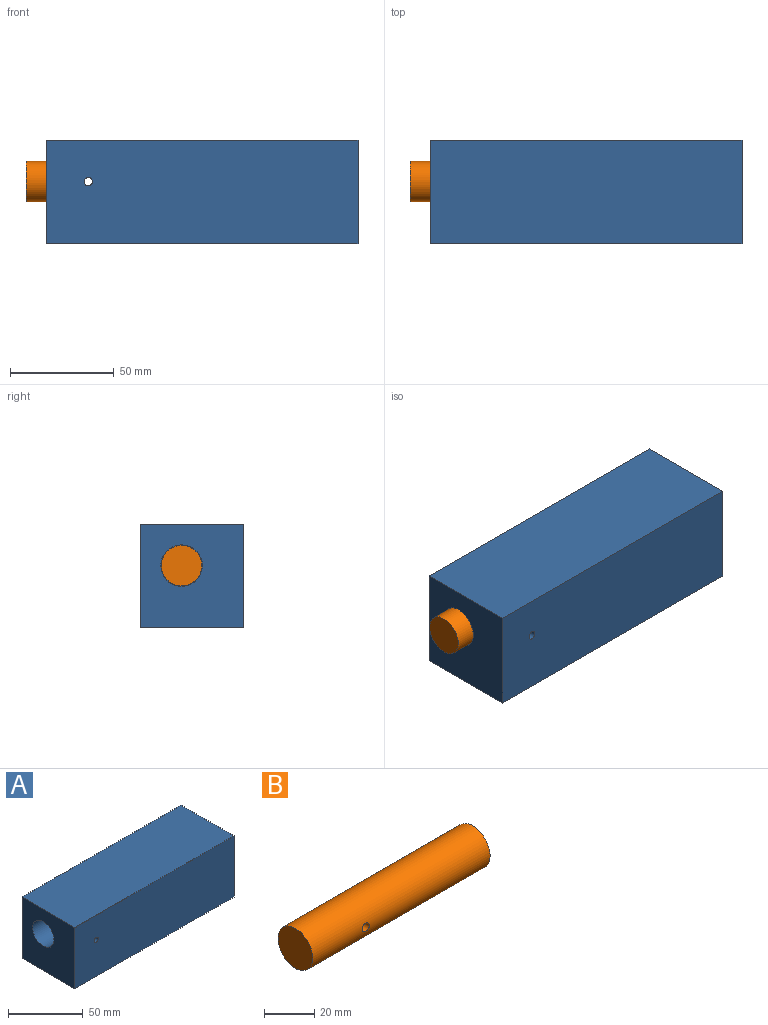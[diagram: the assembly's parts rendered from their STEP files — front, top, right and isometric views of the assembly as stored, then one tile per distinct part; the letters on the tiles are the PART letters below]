
ASSEMBLY  parts=2 mates=1
PART A: 10 faces, bbox 150x50x50 mm
  f0: cylinder r=2mm len=10.2mm, axis (0,-1,0), area 126.9mm2, adj f6,f8
  f1: plane 150x50mm, normal (0,0,1), area 7500mm2, adj f2,f4,f5,f6
  f2: plane 50x50mm, normal (-1,0,0), area 2185.8mm2, adj f1,f3,f5,f6,f8
  f3: plane 150x50mm, normal (0,0,-1), area 7500mm2, adj f2,f4,f5,f6
  f4: plane 50x50mm, normal (1,0,0), area 2500mm2, adj f1,f3,f5,f6
  f5: plane 150x50mm, normal (0,-1,0), area 7487.4mm2, adj f1,f2,f3,f4,f7
  f6: plane 150x50mm, normal (0,1,0), area 7487.4mm2, adj f0,f1,f2,f3,f4
  f7: cylinder r=2mm len=20.2mm, axis (0,-1,0), area 252.6mm2, adj f5,f8
  f8: cylinder r=10mm len=100mm, axis (-1,0,0), area 6257.9mm2, adj f0,f2,f7,f9
  f9: plane 20x20mm, normal (-1,0,0), area 314.2mm2, adj f8
PART B: 4 faces, bbox 100x19.5x19.5 mm
  f0: cylinder r=9.75mm len=100mm, axis (-1,0,0), area 6100.8mm2, adj f1,f2,f3
  f1: plane 19.5x19.5mm, normal (1,0,0), area 298.6mm2, adj f0
  f2: plane 19.5x19.5mm, normal (-1,0,0), area 298.6mm2, adj f0
  f3: cylinder r=2mm len=19.5mm, axis (0,-1,0), area 242.4mm2, adj f0
PLACE A t=(70.67,33.09,-17.9)mm
PLACE B t=(5.69,13.09,12.1)mm
MATE slider A.f8 <-> B.f0  axis (-1,0,0) through (15.65,13.09,12.1)mm
